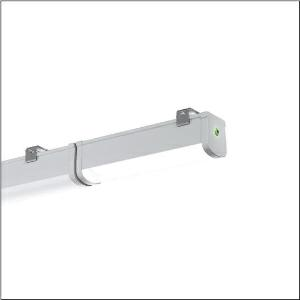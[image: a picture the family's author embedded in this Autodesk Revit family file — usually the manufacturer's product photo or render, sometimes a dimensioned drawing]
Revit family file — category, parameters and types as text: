
# Revit family: monsun_r__31_58fa207a403b3g_c1e4
name_source: partatom
category: Lighting Fixtures
units: mm (PartAtom-declared; Revit-internal decimal feet)

## family parameters
Cut with Voids When Loaded = No
Host = Face
Light Source = No
Part Type = Normal
Room Calculation Point = No
Round Connector Dimension = Use Diameter
Shared = No

## types (1)
- --- (1 x LED, 450 lm, 5 W, 4000K)
    Apparent Load = 5 VA
    CIE Flux Codes = 42 72 91 92 100
    Color Rendering = 80
    Color Temperature = 4000K
    Default Elevation = 1800 mm
    Description = Monsun® 31, emergency light element, primary optical cover: diffuser, of PC, frosted, light emission: direct distribution, primary light characteristic: symmetric, installation type: surface-mounted, EM-KIT 3h,LED, rated luminous flux: 450lm, luminous efficacy: 100lm/W, light colour: 840, colour temperature: 4000K, control gear: without control gear, emergency light function, with socket/plug, mains connection: 220..240V, AC, 50..60Hz, rated input power: 5W, housing, luminaire housing, of PC, light grey (RAL 7035), length: 297mm, width: 68mm, height: 76mm, protection rating (complete): IP65, insulation class (complete): insulation class II (safety insulation), certification: CE, protection symbol: D, impact resistance: IK08, permissible operating ambient temperature: 0..+40°C, standard: EN 60598-2-22, corresponds to IFS (International Featured Standards) requirements for safety and quality in the food industry, packaging unit: 1 piece
    Height = 77 mm
    Lamp = 1 x LED
    Lamp Light Flux = 450 lm
    Lamp Power = 5 W
    Lamp count = 1
    Length = 294 mm
    Luminous efficacy = 90 lm/W
    Manufacturer = Siteco
    ModVariant = No
    Model = 58FA207A403B3G
    Mounting Place = Ceiling
    Mounting Type = Surface mounted
    Number of Poles = 1
    OnlyDefault = Yes
    Power Factor = 1
    Product Name = Monsun® 31
    Product group = emergency light element
    ProductGroupID = 306
    Protection Class = Protection class II
    Protection Degree = IP 65
    RLX_Detail_Level = 1
    RLX_Emergency_Light_Flux = 0 lm
    RLX_Emergency_Type = 0
    RLX_Emergency_Type_DB = No
    RlxData = <blob elided: 31129 chars, md5=567a8a6a>
    Socket = socket
    Standby Power = 0 W
    System Light Flux = 450 lm
    System Power = 5 W
    Type Comments = : 3 h
    Type Image = l_1006658.jpg
    URL = http://relux.com
    VarID = @adj_153653
    Voltage = 0 V
    Weight = 0.00 kg
    Width = 69 mm

## geometry (parser evidence)
native form markers: Blend x4, Sweep x13
no freeform markers — native parametric forms only
